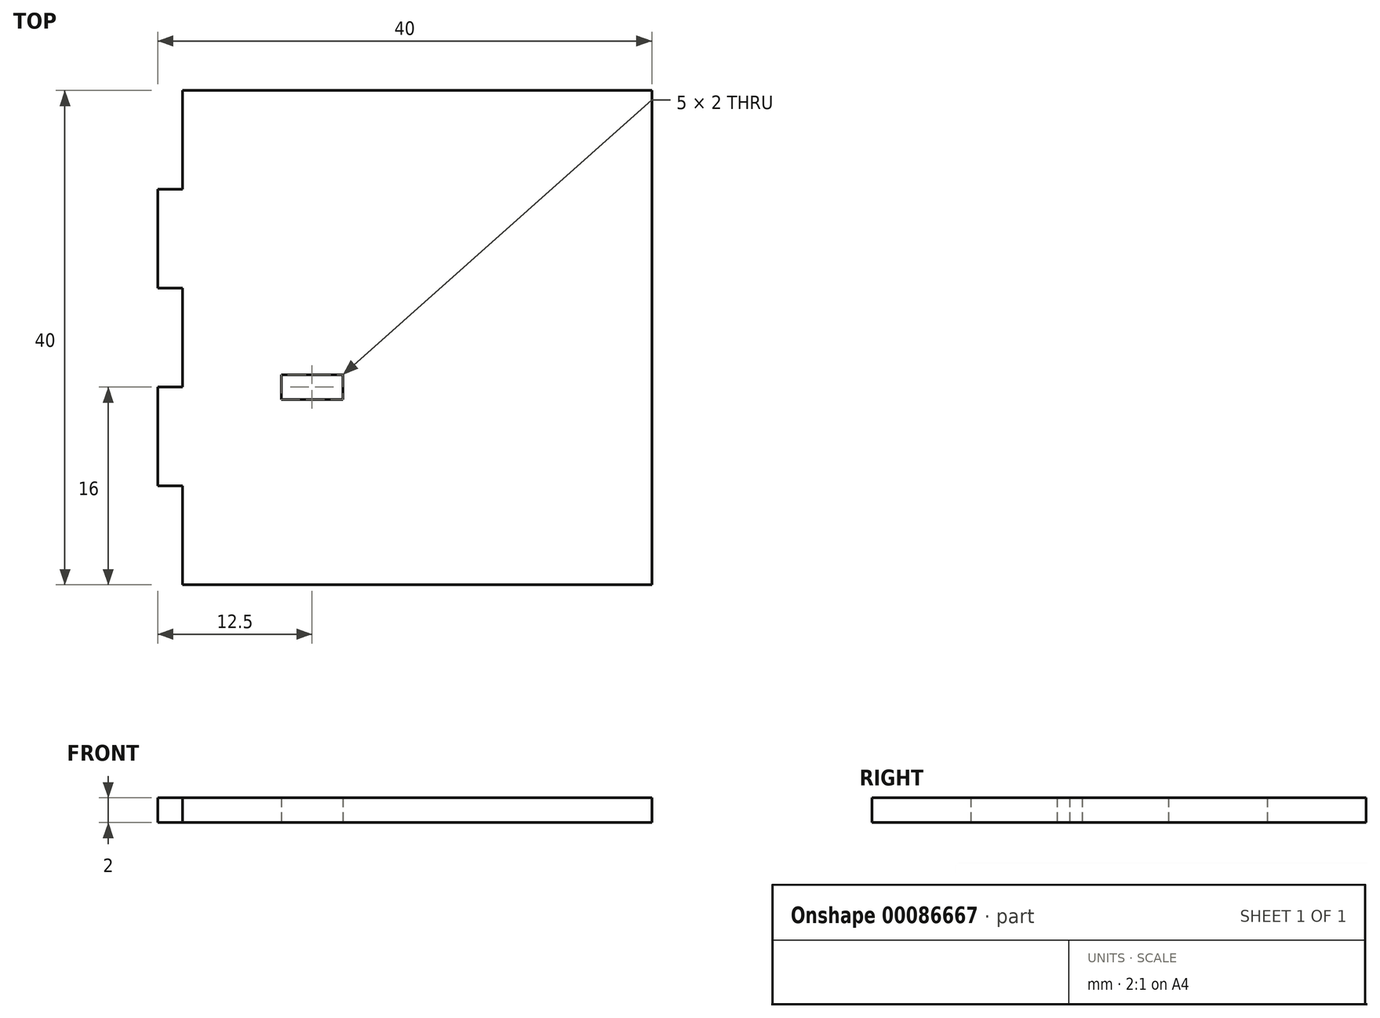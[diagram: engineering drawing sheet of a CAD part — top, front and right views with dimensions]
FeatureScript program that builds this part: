
annotation { "Feature Type Name" : "Feature", "Feature Type Description" : "" }
export const myFeature = defineFeature(function(context is Context, id is Id, definition is map)
    precondition{}
    {
        {
            var Q0;
            Q0=qCreatedBy(makeId("Top.planeOp"),FACE);
            var sketch = newSketch(context, id + "F3", { "sketchPlane" : qUnion([Q0])});
            skLineSegment(sketch, "E0", {"start": v(-2, 0) * mm, "end": v(-2, 40) * mm});
            skLineSegment(sketch, "E1", {"start": v(-2, 40) * mm, "end": v(-40, 40) * mm});
            skLineSegment(sketch, "E2", {"start": v(-40, 40) * mm, "end": v(-40, 32) * mm});
            skLineSegment(sketch, "E3", {"start": v(-40, 32) * mm, "end": v(-42, 32) * mm});
            skLineSegment(sketch, "E4", {"start": v(-42, 32) * mm, "end": v(-42, 24) * mm});
            skLineSegment(sketch, "E5", {"start": v(-42, 24) * mm, "end": v(-40, 24) * mm});
            skLineSegment(sketch, "E6", {"start": v(-40, 24) * mm, "end": v(-40, 16) * mm});
            skLineSegment(sketch, "E7", {"start": v(-40, 16) * mm, "end": v(-42, 16) * mm});
            skLineSegment(sketch, "E8", {"start": v(-42, 16) * mm, "end": v(-42, 8) * mm});
            skLineSegment(sketch, "E9", {"start": v(-42, 8) * mm, "end": v(-40, 8) * mm});
            skLineSegment(sketch, "E10", {"start": v(-40, 8) * mm, "end": v(-40, 0) * mm});
            skLineSegment(sketch, "E11", {"start": v(-40, 0) * mm, "end": v(-2, 0) * mm});
            skSolve(sketch);
        }
        {
            var Q0;
            Q0=makeQuery(id+"F3.imprint","IMPRINT",FACE,{"disambiguationData":[TD([[makeQuery(id+"F3.imprint","IMPRINT",EDGE,{"derivedFrom":sQuery(id+"F3.wireOp",EDGE,"E0")}),1.0]])]});
            var Q1;
            Q1=makeQuery(id+"F3.imprint","IMPRINT",FACE,{"disambiguationData":[TD([[makeQuery(id+"F3.imprint","IMPRINT",EDGE,{"derivedFrom":sQuery(id+"F3.wireOp",EDGE,"06eb4fe1-3f4c-4dfa-b373-b88eca87b1cc")}),1.0]])]});
            var Q2;
            Q2=makeQuery(id+"F3.imprint","IMPRINT",FACE,{"disambiguationData":[TD([[makeQuery(id+"F3.imprint","IMPRINT",EDGE,{"derivedFrom":sQuery(id+"F3.wireOp",EDGE,"e620274a-1ef1-4e1f-b964-3f320ad0e6cd")}),1.0]])]});
            var Q3;
            Q3=makeQuery(id+"F3.imprint","IMPRINT",FACE,{"disambiguationData":[TD([[makeQuery(id+"F3.imprint","IMPRINT",EDGE,{"derivedFrom":sQuery(id+"F3.wireOp",EDGE,"570af66b-53b3-47f8-9f40-16c496dc11be")}),-1.0]])]});
            extrude(context, id + "F0", {"entities" : qUnion([Q0, Q1, Q2, Q3]), "depth" : 2 * mm});
        }
        {
            var Q0;
            Q0=qCreatedBy(makeId("Top.planeOp"),FACE);
            var sketch = newSketch(context, id + "F1", { "sketchPlane" : qUnion([Q0])});
            skLineSegment(sketch, "E12.bottom", {"start": v(-32, 17) * mm, "end": v(-27, 17) * mm});
            skLineSegment(sketch, "E12.top", {"start": v(-32, 15) * mm, "end": v(-27, 15) * mm});
            skLineSegment(sketch, "E12.left", {"start": v(-32, 17) * mm, "end": v(-32, 15) * mm});
            skLineSegment(sketch, "E12.right", {"start": v(-27, 17) * mm, "end": v(-27, 15) * mm});
            skSolve(sketch);
        }
        {
            var Q0;
            Q0=makeQuery(id+"F1.imprint","IMPRINT",FACE,{"disambiguationData":[TD([[makeQuery(id+"F1.imprint","IMPRINT",EDGE,{"derivedFrom":sQuery(id+"F1.wireOp",EDGE,"E12.bottom")}),-1.0]])]});
            extrude(context, id + "F2", {"entities" : qUnion([Q0]), "operationType" : NewBodyOperationType.REMOVE, "depth" : 25 * mm});
        }
    });
